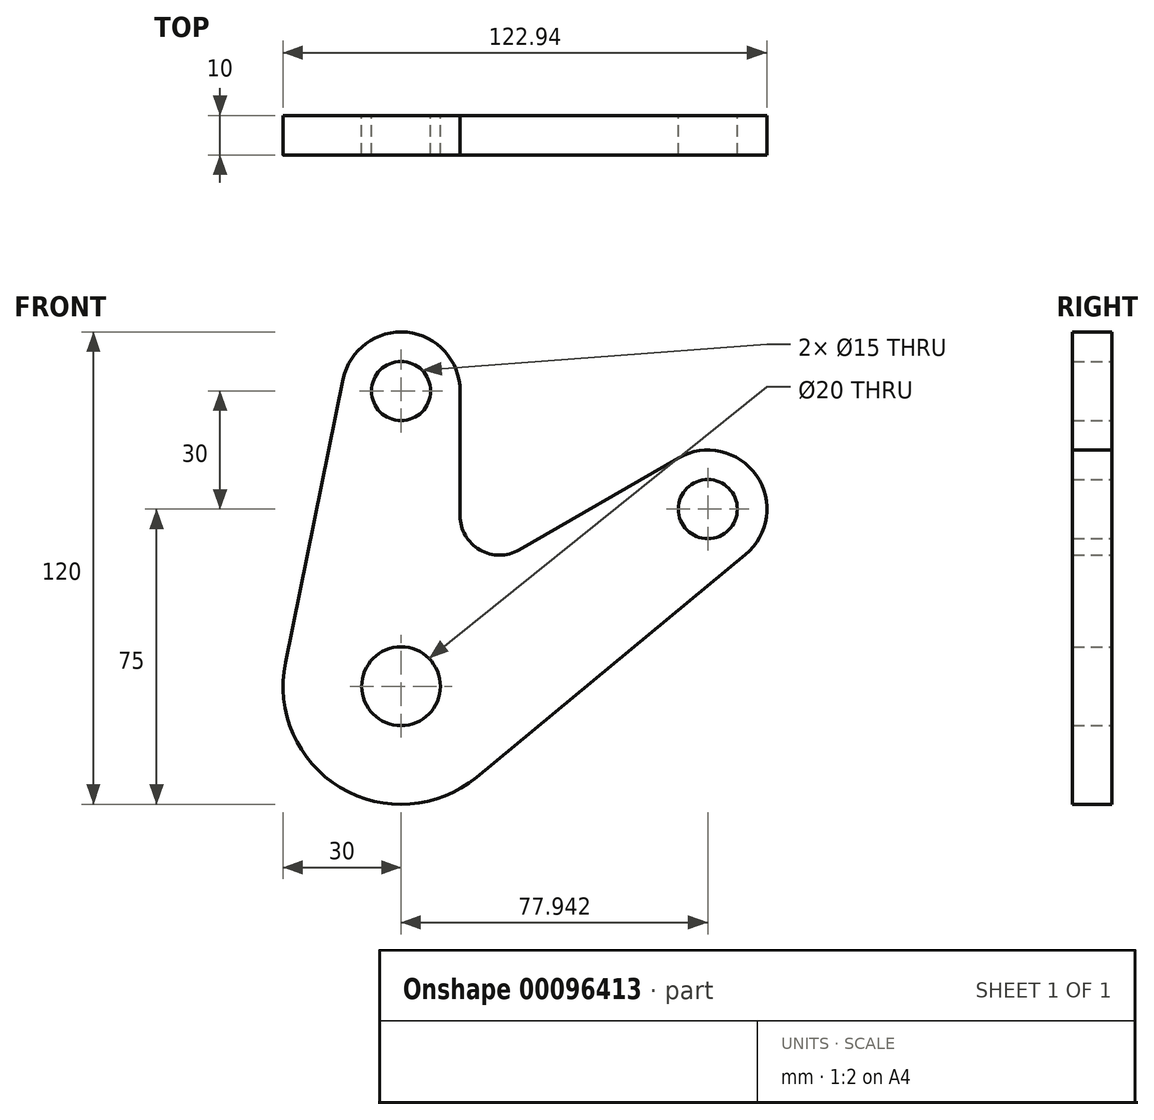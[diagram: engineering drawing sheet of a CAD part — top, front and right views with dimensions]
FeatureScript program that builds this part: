
annotation { "Feature Type Name" : "Feature", "Feature Type Description" : "" }
export const myFeature = defineFeature(function(context is Context, id is Id, definition is map)
    precondition{}
    {
        {
            var Q0;
            Q0=qCreatedBy(makeId("Front.planeOp"),FACE);
            var sketch = newSketch(context, id + "F0", { "sketchPlane" : qUnion([Q0])});
            skCircle(sketch, "E0", {"center": v(0, 0) * mm, "radius": 10 * mm});
            skLineSegment(sketch, "E1", {"start": v(0, 0) * mm, "end": v(0, 75) * mm, "construction": true});
            skCircle(sketch, "E2", {"center": v(0, 75) * mm, "radius": 7.5 * mm});
            skLineSegment(sketch, "E3", {"start": v(0, 0) * mm, "end": v(77.94, 45) * mm, "construction": true});
            skCircle(sketch, "E4", {"center": v(77.94, 45) * mm, "radius": 7.5 * mm});
            skLineSegment(sketch, "E5", {"start": v(15, 75) * mm, "end": v(15, 43.3) * mm});
            skLineSegment(sketch, "E6", {"start": v(-14.7, 78) * mm, "end": v(-29.4, 6) * mm});
            skArc(sketch, "E7", {"start": v(15, 75) * mm, "mid": v(1.5, 89.92) * mm, "end": v(-14.7, 78) * mm});
            skLineSegment(sketch, "E8", {"start": v(30, 34.64) * mm, "end": v(70.44, 58) * mm});
            skArc(sketch, "E9", {"start": v(15, 43.3) * mm, "mid": v(20, 34.64) * mm, "end": v(30, 34.64) * mm});
            skLineSegment(sketch, "E10", {"start": v(87.5, 33.44) * mm, "end": v(19.12, -23.12) * mm});
            skArc(sketch, "E11", {"start": v(87.5, 33.44) * mm, "mid": v(90.26, 53.56) * mm, "end": v(70.44, 58) * mm});
            skArc(sketch, "E12", {"start": v(-29.4, 6) * mm, "mid": v(-15.44, -25.72) * mm, "end": v(19.12, -23.12) * mm});
            skSolve(sketch);
        }
        {
            var Q0;
            Q0=makeQuery(id+"F0.imprint","IMPRINT",FACE,{"disambiguationData":[TD([[makeQuery(id+"F0.imprint","IMPRINT",EDGE,{"derivedFrom":sQuery(id+"F0.wireOp",EDGE,"E0")}),-1.0]])]});
            extrude(context, id + "F1", {"entities" : qUnion([Q0]), "depth" : 10 * mm});
        }
    });
